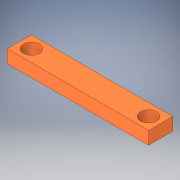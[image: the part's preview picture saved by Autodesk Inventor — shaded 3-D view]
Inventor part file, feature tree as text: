
AUTODESK INVENTOR PART (.ipt)
format: ipt  version: 2019 (Build 230136000, 136)  size: 117,248 bytes
history: native  units: mm
features: extrude x1, sketch x1
ambient origin geometry x8: Origin, YZ Plane, XZ Plane, XY Plane, X Axis, Y Axis, Z Axis, Center Point
bodies: Solid1 (feature_tree)
feature tree (2):
  extrude  "Extrusion1"  Depth=6.0mm
  sketch  "Sketch1"  dims[d0=35.0mm d1=6.0mm d2=4.0mm d3=4.0mm d4=3.0mm d5=3.0mm d6=3.0mm d7=3.0mm d8=3.18mm d9=0.0mm]
